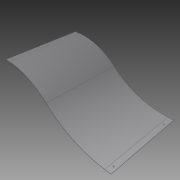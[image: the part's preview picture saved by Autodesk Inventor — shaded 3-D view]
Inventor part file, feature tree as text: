
AUTODESK INVENTOR PART (.ipt)
format: ipt  version: 2014 SP1 (Build 180222100, 222)  size: 109,568 bytes
history: native  units: in
note: dims shown in document units (in); Inventor stores cm internally (conversion verified against a paired STEP export)
features: reference x5, extrude x3, sketch x3, plane x1
ambient origin geometry x8: Origin, YZ Plane, XZ Plane, XY Plane, X Axis, Y Axis, Z Axis, Center Point
bodies: Solid1 (feature_tree)
feature tree (12):
  plane  "Work Plane1"
  extrude  "Extrusion1"  Depth=8.5in TaperAngle=0.0deg
  extrude  "Extrusion2"  Depth=5.0in
  extrude  "Extrusion3"  [1 undecoded]
  sketch  "Sketch1"  dims[d2=8.5in d3=0.0in d4=10.0in d5=0.0in]
  reference  "Reference1"
  reference  "Reference2"
  reference  "Reference3"
  sketch  "Sketch2"  dims[d6=10.0in d7=0.0in d8=5.0in]
  sketch  "Sketch3"  dims[d9=0.0312in]
  reference  "Reference7"
  reference  "Reference8"
note: 1 required parameter value undecoded (feature->parameter linkage not recoverable at this tier; creation-order binding heuristic only, values carry confidence <= 0.55)
